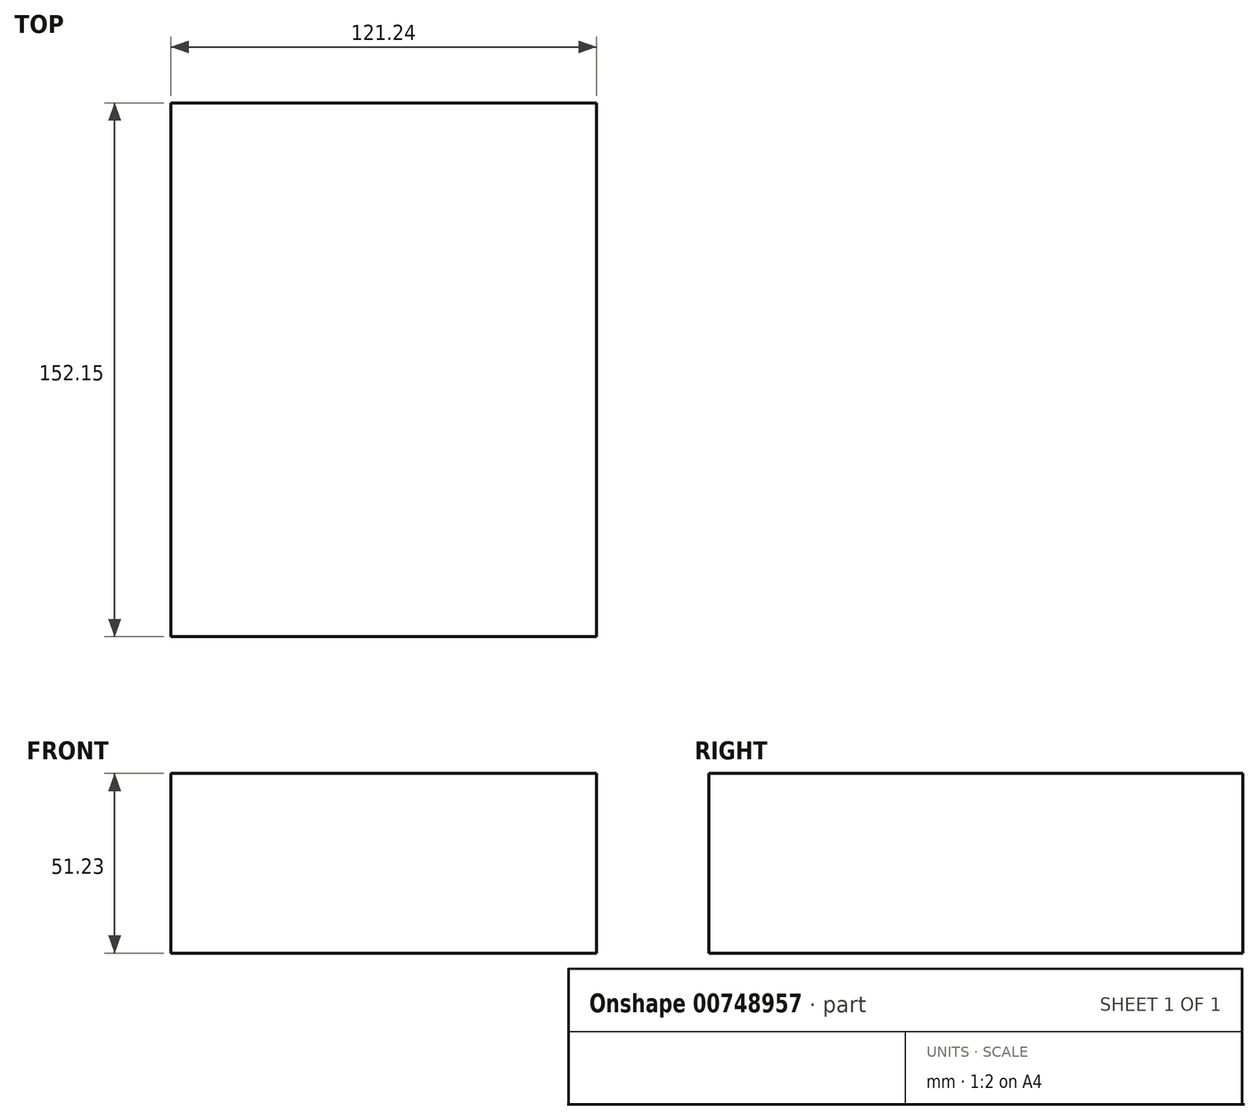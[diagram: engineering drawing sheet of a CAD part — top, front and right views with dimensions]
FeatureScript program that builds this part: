
annotation { "Feature Type Name" : "Feature", "Feature Type Description" : "" }
export const myFeature = defineFeature(function(context is Context, id is Id, definition is map)
    precondition{}
    {
        {
            var Q0;
            Q0=qCreatedBy(makeId("Front.planeOp"),FACE);
            var sketch = newSketch(context, id + "F0", { "sketchPlane" : qUnion([Q0])});
            skLineSegment(sketch, "E0.bottom", {"start": v(-121.24, 0) * mm, "end": v(0, 0) * mm});
            skLineSegment(sketch, "E0.top", {"start": v(-121.24, -51.23) * mm, "end": v(0, -51.23) * mm});
            skLineSegment(sketch, "E0.left", {"start": v(-121.24, 0) * mm, "end": v(-121.24, -51.23) * mm});
            skLineSegment(sketch, "E0.right", {"start": v(0, 0) * mm, "end": v(0, -51.23) * mm});
            skSolve(sketch);
        }
        {
            var Q0;
            Q0 = qSketchRegion(id + "F0", true);
            extrude(context, id + "F1", {"entities" : qUnion([Q0]), "oppositeDirection" : true, "depth" : 152.15 * mm, "offsetDistance" : 25.4 * mm});
        }
    });
